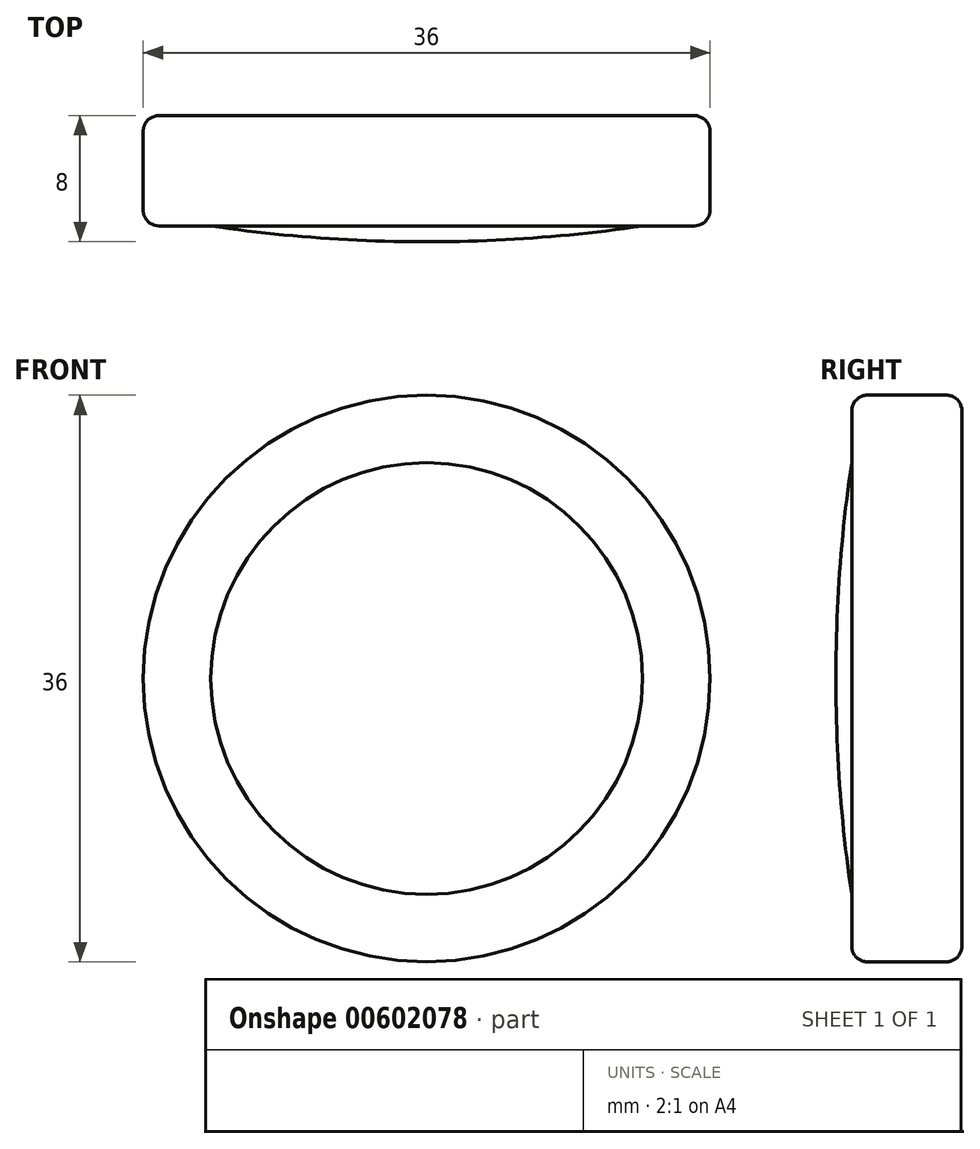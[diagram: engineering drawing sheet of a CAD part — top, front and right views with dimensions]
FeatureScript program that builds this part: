
annotation { "Feature Type Name" : "Feature", "Feature Type Description" : "" }
export const myFeature = defineFeature(function(context is Context, id is Id, definition is map)
    precondition{}
    {
        {
            var Q0;
            Q0=qCreatedBy(makeId("Front.planeOp"),FACE);
            var sketch = newSketch(context, id + "F0", { "sketchPlane" : qUnion([Q0])});
            skCircle(sketch, "E0", {"center": v(0, 0) * mm, "radius": 18 * mm});
            skCircle(sketch, "E1", {"center": v(0, 0) * mm, "radius": 13.67 * mm});
            skSolve(sketch);
        }
        {
            var Q0;
            Q0=makeQuery(id+"F0.imprint","IMPRINT",FACE,{"disambiguationData":[TD([[makeQuery(id+"F0.imprint","IMPRINT",EDGE,{"derivedFrom":sQuery(id+"F0.wireOp",EDGE,"E0")}),1.0]])]});
            extrude(context, id + "F1", {"entities" : qUnion([Q0]), "depth" : 7 * mm, "offsetDistance" : 25 * mm});
        }
        {
            var Q0;
            Q0=makeQuery(id+"F1.opExtrude","CAP_EDGE",EDGE,{"disambiguationData":[OSD([sQuery(id+"F0.wireOp",EDGE,"E0")])],"isStart":false});
            var Q1;
            Q1=makeQuery(id+"F1.opExtrude","CAP_EDGE",EDGE,{"disambiguationData":[OSD([sQuery(id+"F0.wireOp",EDGE,"E0")])],"isStart":true});
            fillet(context, id + "F2", {"entities" : qUnion([Q0, Q1]), "radius" : 1 * mm, "tangentPropagation" : true, "allowEdgeOverflow" : false});
        }
        {
            var Q0;
            Q0=qCreatedBy(makeId("Front.planeOp"),FACE);
            var sketch = newSketch(context, id + "F3", { "sketchPlane" : qUnion([Q0])});
            skCircle(sketch, "E2", {"center": v(0, 0) * mm, "radius": 13.7 * mm});
            skSolve(sketch);
        }
        {
            var Q0;
            Q0 = qSketchRegion(id + "F3", true);
            extrude(context, id + "F4", {"entities" : qUnion([Q0]), "operationType" : NewBodyOperationType.ADD, "depth" : 8 * mm, "offsetDistance" : 25 * mm});
        }
        {
            var Q0;
            Q0=makeQuery(id+"F4.opExtrude","CAP_EDGE",EDGE,{"disambiguationData":[OSD([sQuery(id+"F3.wireOp",EDGE,"E2")])],"isStart":false});
            fillet(context, id + "F5", {"entities" : qUnion([Q0]), "radius" : 90 * mm, "tangentPropagation" : true, "allowEdgeOverflow" : false});
        }
    });
